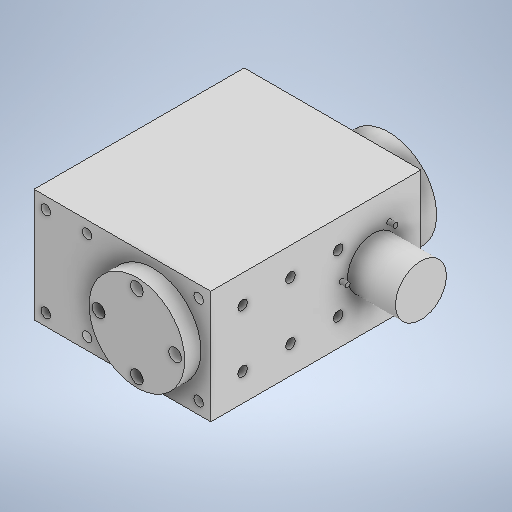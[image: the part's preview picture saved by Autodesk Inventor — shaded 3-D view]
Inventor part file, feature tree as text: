
AUTODESK INVENTOR PART (.ipt)
format: ipt  version: 2025.1 (Build 291241000, 241)  size: 339,968 bytes
history: native  units: mm
features: extrude x5, sketch x4, hole x2, other x2, mirror x1
ambient origin geometry x8: Origin, YZ Plane, XZ Plane, XY Plane, X Axis, Y Axis, Z Axis, Center Point
bodies: Solide1 (feature_tree)
feature tree (14):
  extrude  "Extrusion1"  Depth=66.0mm
  sketch  "Esquisse2"
  hole  "Perçage1"  [1 undecoded]
  mirror  "Mise en miroir1"
  extrude  "Extrusion2"  Depth=35.5mm TaperAngle=0.0deg
  extrude  "Extrusion3"  Depth=18.0mm
  sketch  "Esquisse4"
  extrude  "Extrusion4"  Depth=3.0mm
  hole  "Perçage2"  [1 undecoded]
  extrude  "Extrusion5"  Depth=1.5mm
  sketch  "Esquisse1"
  other  "Réseau d'esquisse circulaire2"
  sketch  "Esquisse5"
  other  "Réseau d'esquisse circulaire3"
note: 2 required parameter values undecoded (feature->parameter linkage not recoverable at this tier; creation-order binding heuristic only, values carry confidence <= 0.55)
